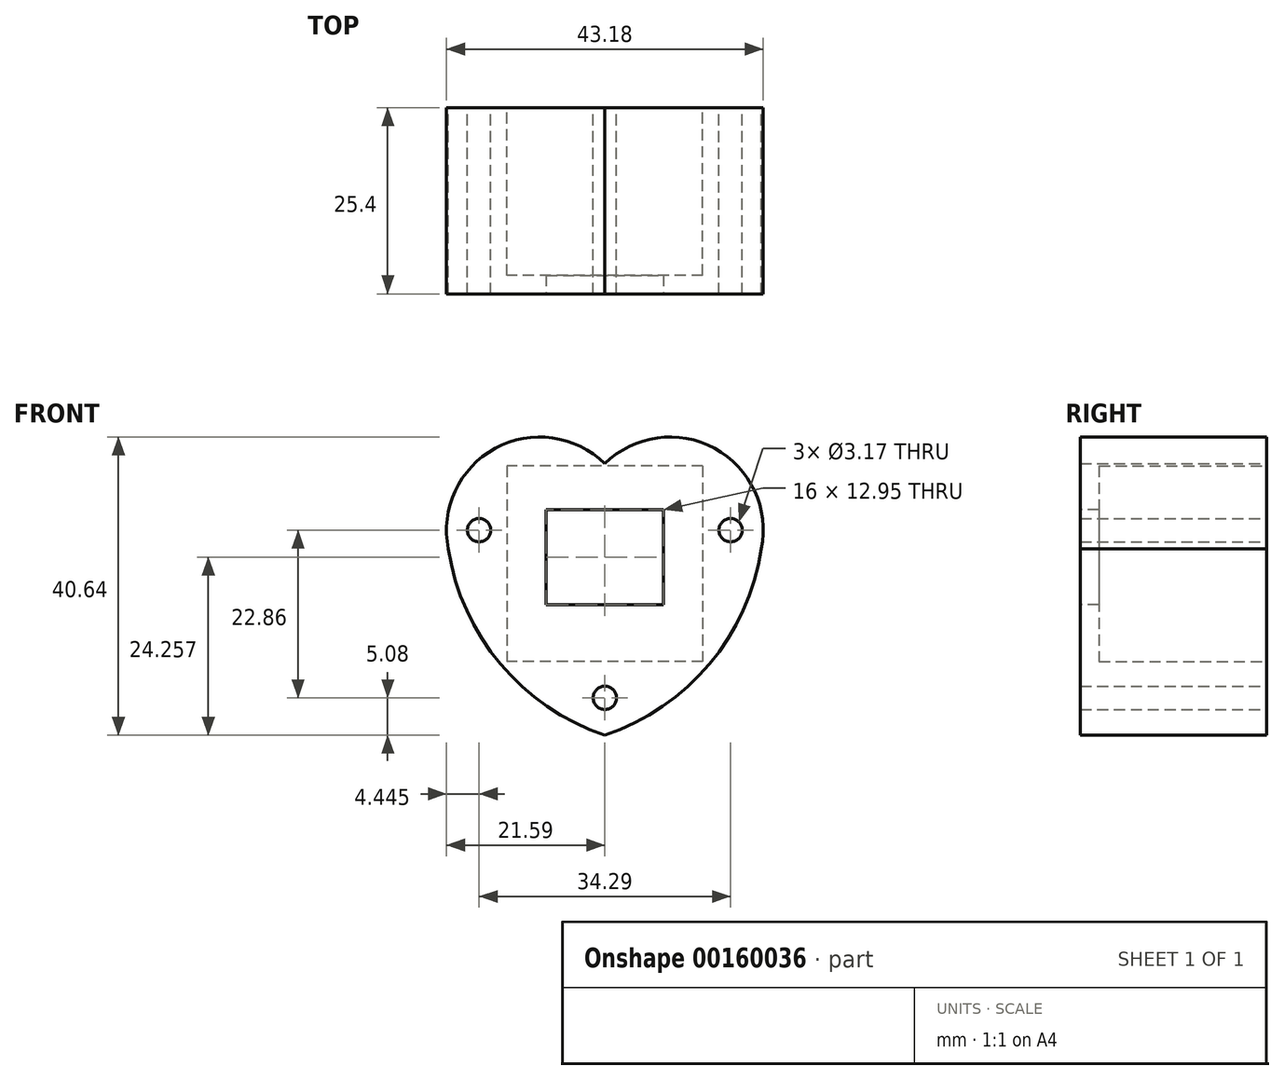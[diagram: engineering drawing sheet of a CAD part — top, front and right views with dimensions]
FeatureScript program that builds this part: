
annotation { "Feature Type Name" : "Feature", "Feature Type Description" : "" }
export const myFeature = defineFeature(function(context is Context, id is Id, definition is map)
    precondition{}
    {
        {
            var Q0;
            Q0=qCreatedBy(makeId("Front.planeOp"),FACE);
            var sketch = newSketch(context, id + "F0", { "sketchPlane" : qUnion([Q0])});
            skArc(sketch, "E0", {"start": v(21.33, 6.35) * mm, "mid": v(14.96, 20.05) * mm, "end": v(0, 17.96) * mm});
            skArc(sketch, "E1", {"start": v(0, 17.96) * mm, "mid": v(-14.96, 20.05) * mm, "end": v(-21.33, 6.35) * mm});
            skLineSegment(sketch, "E2", {"start": v(-46.66, 6.35) * mm, "end": v(72.33, 6.35) * mm, "construction": true});
            skArc(sketch, "E3", {"start": v(-21.33, 6.35) * mm, "mid": v(-14.25, -9.36) * mm, "end": v(0, -19.05) * mm});
            skArc(sketch, "E4", {"start": v(0, -19.05) * mm, "mid": v(14.25, -9.36) * mm, "end": v(21.33, 6.35) * mm});
            skSolve(sketch);
        }
        {
            var Q0;
            Q0 = qSketchRegion(id + "F0", true);
            extrude(context, id + "F1", {"entities" : qUnion([Q0]), "depth" : 25.4 * mm});
        }
        {
            var Q0;
            Q0=makeQuery(id+"F1.opExtrude","CAP_FACE",FACE,{"disambiguationData":[OSD([sQuery(id+"F0.wireOp",EDGE,"E0"),sQuery(id+"F0.wireOp",EDGE,"E1"),sQuery(id+"F0.wireOp",EDGE,"E3"),sQuery(id+"F0.wireOp",EDGE,"E4")])],"isStart":false});
            var sketch = newSketch(context, id + "F2", { "sketchPlane" : qUnion([Q0])});
            skLineSegment(sketch, "E5.bottom", {"start": v(-8, 11.68) * mm, "end": v(8, 11.68) * mm});
            skLineSegment(sketch, "E5.top", {"start": v(-8, -1.27) * mm, "end": v(8, -1.27) * mm});
            skLineSegment(sketch, "E5.left", {"start": v(-8, 11.68) * mm, "end": v(-8, -1.27) * mm});
            skLineSegment(sketch, "E5.right", {"start": v(8, 11.68) * mm, "end": v(8, -1.27) * mm});
            skSolve(sketch);
        }
        {
            var Q0;
            Q0 = qSketchRegion(id + "F2", true);
            extrude(context, id + "F3", {"entities" : qUnion([Q0]), "operationType" : NewBodyOperationType.REMOVE, "endBound" : BoundingType.THROUGH_ALL, "oppositeDirection" : true, "depth" : 25.4 * mm});
        }
        {
            var Q0;
            Q0=makeQuery(id+"F1.opExtrude","CAP_FACE",FACE,{"disambiguationData":[OSD([sQuery(id+"F0.wireOp",EDGE,"E0"),sQuery(id+"F0.wireOp",EDGE,"E1"),sQuery(id+"F0.wireOp",EDGE,"E3"),sQuery(id+"F0.wireOp",EDGE,"E4")])],"isStart":true});
            var sketch = newSketch(context, id + "F4", { "sketchPlane" : qUnion([Q0])});
            skLineSegment(sketch, "E6.bottom", {"start": v(-13.34, 17.65) * mm, "end": v(13.34, 17.65) * mm});
            skLineSegment(sketch, "E6.top", {"start": v(-13.34, -9.02) * mm, "end": v(13.34, -9.02) * mm});
            skLineSegment(sketch, "E6.left", {"start": v(-13.33, 17.65) * mm, "end": v(-13.34, -9.02) * mm});
            skLineSegment(sketch, "E6.right", {"start": v(13.34, 17.65) * mm, "end": v(13.33, -9.02) * mm});
            skSolve(sketch);
        }
        {
            var Q0;
            Q0 = qSketchRegion(id + "F4", true);
            extrude(context, id + "F5", {"entities" : qUnion([Q0]), "operationType" : NewBodyOperationType.REMOVE, "oppositeDirection" : true, "depth" : 22.86 * mm});
        }
        {
            var Q0;
            Q0=makeQuery(id+"F1.opExtrude","CAP_FACE",FACE,{"disambiguationData":[OSD([sQuery(id+"F0.wireOp",EDGE,"E0"),sQuery(id+"F0.wireOp",EDGE,"E1"),sQuery(id+"F0.wireOp",EDGE,"E3"),sQuery(id+"F0.wireOp",EDGE,"E4")])],"isStart":true});
            var sketch = newSketch(context, id + "F6", { "sketchPlane" : qUnion([Q0])});
            skCircle(sketch, "E7", {"center": v(-17.15, 8.9) * mm, "radius": 1.59 * mm});
            skCircle(sketch, "E8", {"center": v(17.15, 8.9) * mm, "radius": 1.59 * mm});
            skCircle(sketch, "E9", {"center": v(0, -13.97) * mm, "radius": 1.59 * mm});
            skSolve(sketch);
        }
        {
            var Q0;
            Q0 = qSketchRegion(id + "F6", true);
            extrude(context, id + "F7", {"entities" : qUnion([Q0]), "operationType" : NewBodyOperationType.REMOVE, "endBound" : BoundingType.THROUGH_ALL, "oppositeDirection" : true, "depth" : 25.4 * mm});
        }
    });
